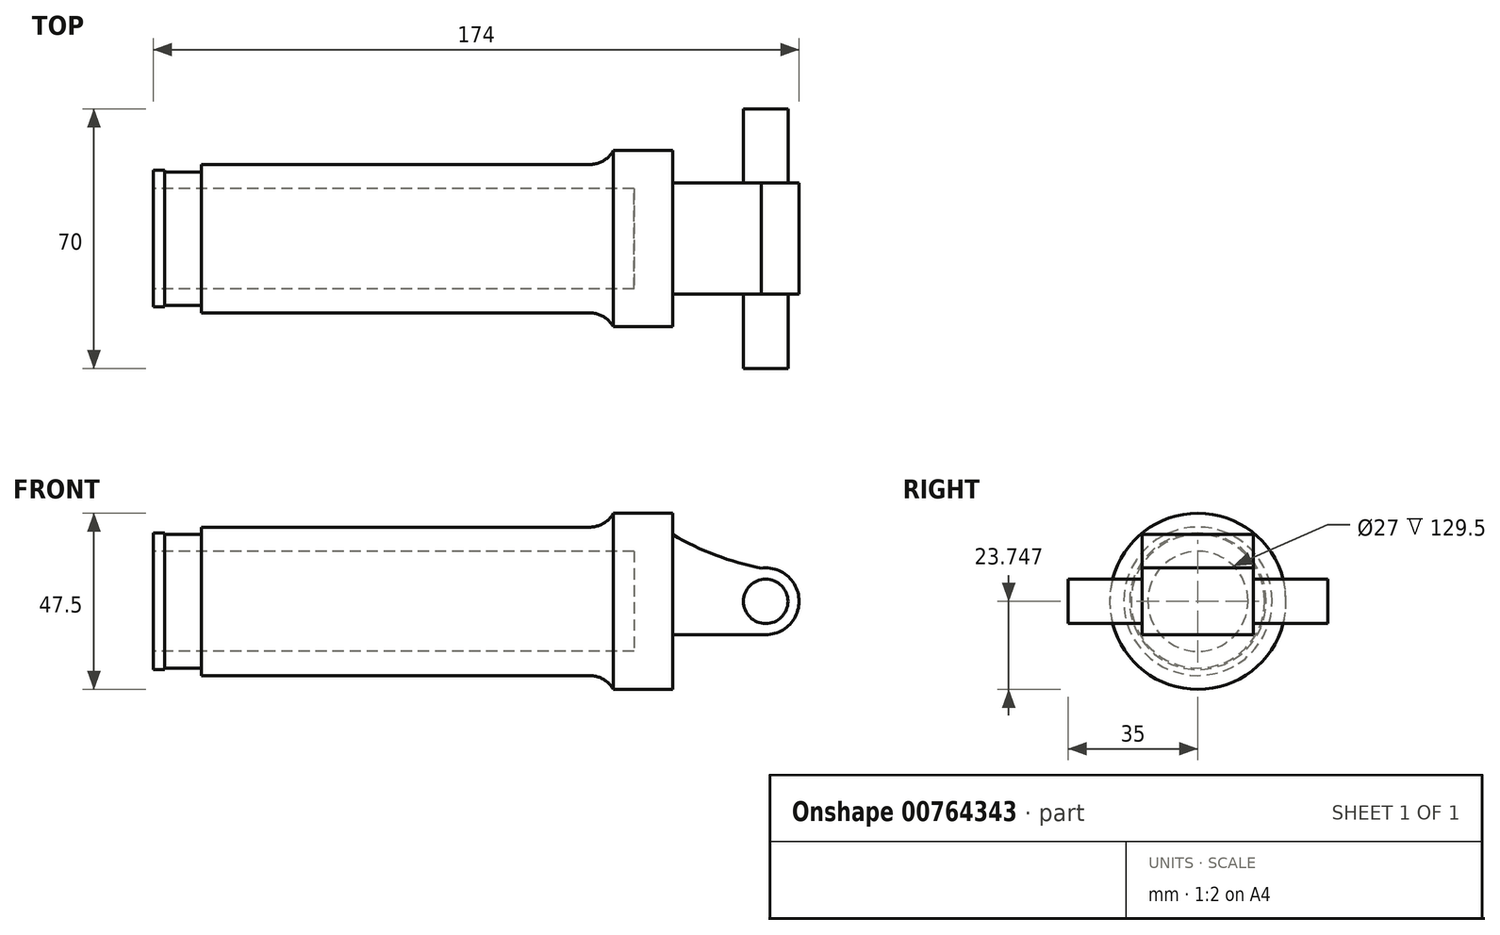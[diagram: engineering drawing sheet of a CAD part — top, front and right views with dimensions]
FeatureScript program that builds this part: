
annotation { "Feature Type Name" : "Feature", "Feature Type Description" : "" }
export const myFeature = defineFeature(function(context is Context, id is Id, definition is map)
    precondition{}
    {
        {
            var Q0;
            Q0=qCreatedBy(makeId("Front.planeOp"),FACE);
            var sketch = newSketch(context, id + "F0", { "sketchPlane" : qUnion([Q0])});
            skLineSegment(sketch, "E0", {"start": v(-148.22, 37.86) * mm, "end": v(109.78, 37.86) * mm, "construction": true});
            skCircle(sketch, "E1", {"center": v(109.78, 37.86) * mm, "radius": 9 * mm});
            skLineSegment(sketch, "E2", {"start": v(-55.22, 56.26) * mm, "end": v(-52.22, 56.26) * mm});
            skLineSegment(sketch, "E3", {"start": v(-52.22, 56.26) * mm, "end": v(-52.22, 55.86) * mm});
            skLineSegment(sketch, "E4", {"start": v(-52.22, 55.86) * mm, "end": v(-42.22, 55.86) * mm});
            skLineSegment(sketch, "E5", {"start": v(-42.22, 55.86) * mm, "end": v(-42.22, 57.86) * mm});
            skLineSegment(sketch, "E6", {"start": v(-42.22, 57.86) * mm, "end": v(62.28, 57.86) * mm});
            skLineSegment(sketch, "E7", {"start": v(84.78, 37.86) * mm, "end": v(84.78, 61.6) * mm});
            skLineSegment(sketch, "E8", {"start": v(84.78, 61.6) * mm, "end": v(68.78, 61.6) * mm});
            skArc(sketch, "E9", {"start": v(62.28, 57.86) * mm, "mid": v(66.04, 58.86) * mm, "end": v(68.78, 61.6) * mm});
            skLineSegment(sketch, "E10", {"start": v(-55.22, 37.86) * mm, "end": v(84.78, 37.86) * mm});
            skLineSegment(sketch, "E11.bottom", {"start": v(-55.22, 51.36) * mm, "end": v(-43.22, 51.36) * mm});
            skLineSegment(sketch, "E11.top", {"start": v(-55.22, 37.86) * mm, "end": v(-43.22, 37.86) * mm});
            skLineSegment(sketch, "E11.right", {"start": v(-43.22, 51.36) * mm, "end": v(-43.22, 37.86) * mm});
            skLineSegment(sketch, "E12.bottom", {"start": v(-43.22, 51.36) * mm, "end": v(68.78, 51.36) * mm});
            skLineSegment(sketch, "E12.top", {"start": v(-43.22, 37.86) * mm, "end": v(68.78, 37.86) * mm});
            skLineSegment(sketch, "E12.right", {"start": v(68.78, 51.36) * mm, "end": v(68.78, 37.86) * mm});
            skLineSegment(sketch, "E13", {"start": v(84.78, 37.86) * mm, "end": v(84.78, 28.86) * mm});
            skLineSegment(sketch, "E14", {"start": v(109.78, 28.86) * mm, "end": v(84.78, 28.86) * mm});
            skArc(sketch, "E15", {"start": v(84.78, 55.86) * mm, "mid": v(96.48, 50.23) * mm, "end": v(108.97, 46.7) * mm});
            skLineSegment(sketch, "E16", {"start": v(-55.22, 56.26) * mm, "end": v(-55.22, 37.86) * mm});
            skSolve(sketch);
        }
        {
            var Q0;
            {var subQ4=sQuery(id+"F0.wireOp",EDGE,"E2");Q0=makeQuery(id+"F0.imprint","IMPRINT",FACE,{"disambiguationData":[TD([[makeQuery(id+"F0.imprint","IMPRINT",EDGE,{"derivedFrom":subQ4}),-1.0]])]});}
            var Q1;
            Q1=makeQuery(id+"F0.imprint","IMPRINT",FACE,{"disambiguationData":[TD([[makeQuery(id+"F0.imprint","IMPRINT",EDGE,{"derivedFrom":sQuery(id+"F0.wireOp",EDGE,"E12.bottom")}),-1.0]])]});
            var Q2;
            Q2=sQuery(id+"F0.wireOp",EDGE,"E10");
            revolve(context, id + "F1", {"surfaceOperationType" : NewSurfaceOperationType.NEW, "entities" : qUnion([Q0, Q1]), "axis" : qUnion([Q2]), "revolveType" : RevolveType.FULL});
        }
        {
            var Q0;
            Q0=makeQuery(id+"F1.opRevolve","SWEPT_FACE",FACE,{"disambiguationData":[OSD([sQuery(id+"F0.wireOp",EDGE,"E11.right")])]});
            extrude(context, id + "F2", {"entities" : qUnion([Q0]), "operationType" : NewBodyOperationType.REMOVE, "oppositeDirection" : true, "depth" : 117.5 * mm, "offsetDistance" : 25 * mm});
        }
        {
            var Q0;
            {var subQ1=sQuery(id+"F0.wireOp",EDGE,"E13");Q0=makeQuery(id+"F0.imprint","IMPRINT",FACE,{"disambiguationData":[TD([[makeQuery(id+"F0.imprint","IMPRINT",EDGE,{"derivedFrom":subQ1}),1.0]])]});}
            var Q1;
            {var subQ0=sQuery(id+"F0.wireOp",EDGE,"E1");var subQ1=makeQuery(id+"F0.imprint","INTERSECT",VERTEX,{"derivedFrom":[subQ0,sQuery(id+"F0.wireOp",EDGE,"E14")]});Q1=makeQuery(id+"F0.imprint","IMPRINT",FACE,{"disambiguationData":[TD([[makeQuery(id+"F0.imprint","IMPRINT",EDGE,{"disambiguationData":[TD([[subQ1,1.0]])],"derivedFrom":subQ0}),1.0]])]});}
            extrude(context, id + "F3", {"entities" : qUnion([Q0, Q1]), "operationType" : NewBodyOperationType.ADD, "endBound" : BoundingType.SYMMETRIC, "depth" : 30 * mm, "offsetDistance" : 25 * mm});
        }
        {
            var Q0;
            Q0=makeQuery(id+"F3.opExtrude","CAP_FACE",FACE,{"disambiguationData":[OSD([sQuery(id+"F0.wireOp",EDGE,"E1"),sQuery(id+"F0.wireOp",EDGE,"E7"),sQuery(id+"F0.wireOp",EDGE,"E13"),sQuery(id+"F0.wireOp",EDGE,"E14"),sQuery(id+"F0.wireOp",EDGE,"E15")])],"isStart":false});
            var sketch = newSketch(context, id + "F4", { "sketchPlane" : qUnion([Q0])});
            skCircle(sketch, "E17", {"center": v(109.78, 37.86) * mm, "radius": 6 * mm});
            skSolve(sketch);
        }
        {
            var Q0;
            Q0 = qSketchRegion(id + "F4", true);
            extrude(context, id + "F5", {"entities" : qUnion([Q0]), "operationType" : NewBodyOperationType.ADD, "depth" : 20 * mm, "offsetDistance" : 25 * mm});
        }
        {
            var Q0;
            Q0=makeQuery(id+"F5.opExtrude","CAP_FACE",FACE,{"disambiguationData":[OSD([sQuery(id+"F4.wireOp",EDGE,"E17")])],"isStart":false});
            extrude(context, id + "F6", {"entities" : qUnion([Q0]), "operationType" : NewBodyOperationType.ADD, "oppositeDirection" : true, "depth" : 70 * mm, "offsetDistance" : 25 * mm});
        }
    });
